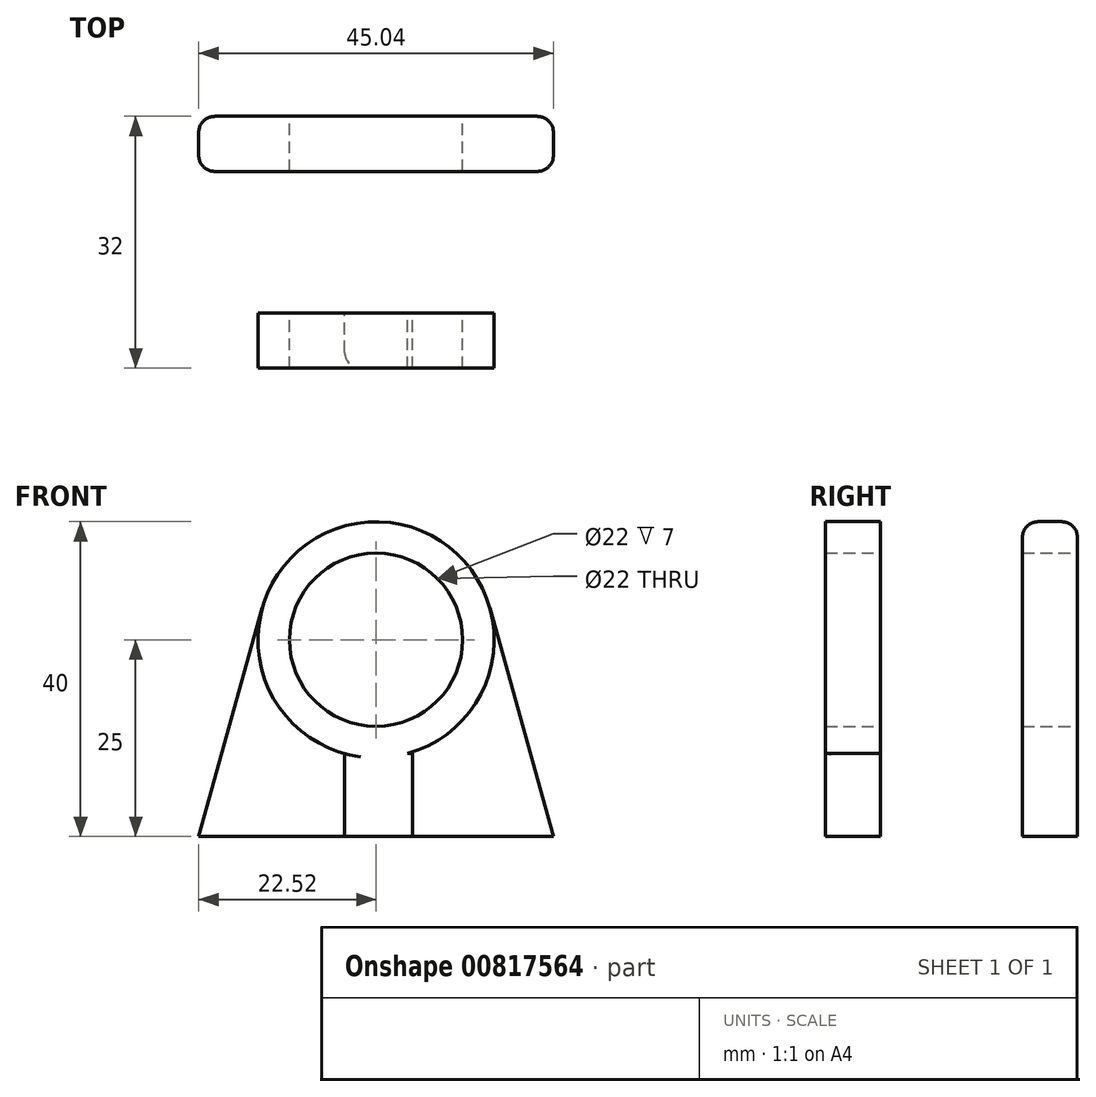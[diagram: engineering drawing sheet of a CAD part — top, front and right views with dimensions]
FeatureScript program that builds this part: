
annotation { "Feature Type Name" : "Feature", "Feature Type Description" : "" }
export const myFeature = defineFeature(function(context is Context, id is Id, definition is map)
    precondition{}
    {
        {
            var Q0;
            Q0=qCreatedBy(makeId("Front.planeOp"),FACE);
            var sketch = newSketch(context, id + "F0", { "sketchPlane" : qUnion([Q0])});
            skCircle(sketch, "E0", {"center": v(0, 25) * mm, "radius": 11 * mm});
            skCircle(sketch, "E1", {"center": v(0, 25) * mm, "radius": 15 * mm});
            skLineSegment(sketch, "E2", {"start": v(-14.45, 29.02) * mm, "end": v(-22.52, 0) * mm});
            skLineSegment(sketch, "E3", {"start": v(-22.52, 0) * mm, "end": v(0, 0) * mm});
            skLineSegment(sketch, "E4", {"start": v(0, 0) * mm, "end": v(0, 11.14) * mm, "construction": true});
            skLineSegment(sketch, "E5.MirrorCS", {"start": v(14.45, 29.02) * mm, "end": v(22.52, 0) * mm});
            skLineSegment(sketch, "E6.MirrorCS", {"start": v(22.52, 0) * mm, "end": v(0, 0) * mm});
            skSolve(sketch);
        }
        {
            assignVariable(context, id + "F1", {"name" : "Thickness", "anyValue" : 7 * mm});
        }
        {
            var Q0;
            {var subQ1=sQuery(id+"F0.wireOp",EDGE,"E2");Q0=makeQuery(id+"F0.imprint","IMPRINT",FACE,{"disambiguationData":[TD([[makeQuery(id+"F0.imprint","IMPRINT",EDGE,{"derivedFrom":subQ1}),1.0]])]});}
            var Q1;
            Q1=makeQuery(id+"F0.imprint","IMPRINT",FACE,{"disambiguationData":[TD([[makeQuery(id+"F0.imprint","IMPRINT",EDGE,{"derivedFrom":sQuery(id+"F0.wireOp",EDGE,"E0")}),-1.0]])]});
            extrude(context, id + "F2", {"entities" : qUnion([Q0, Q1]), "depth" : getVariable(context, 'Thickness'), "offsetDistance" : 25 * mm});
        }
        {
            var Q0;
            Q0=qCreatedBy(makeId("Front.planeOp"),FACE);
            cPlane(context, id + "F3", {"entities" : qUnion([Q0]), "cplaneType" : CPlaneType.OFFSET, "offset" : 25 * mm, "width" : 150 * mm, "height" : 150 * mm});
        }
        {
            var Q0;
            Q0=qCreatedBy(id+"F3.planeOp",FACE);
            var sketch = newSketch(context, id + "F4", { "sketchPlane" : qUnion([Q0])});
            skCircle(sketch, "E7.0", {"center": v(0, 25) * mm, "radius": 11 * mm});
            skCircle(sketch, "E8", {"center": v(0, 25) * mm, "radius": 15 * mm});
            skLineSegment(sketch, "E9.bottom", {"start": v(-3.98, 10.54) * mm, "end": v(4.64, 10.54) * mm});
            skLineSegment(sketch, "E9.top", {"start": v(-3.98, 0) * mm, "end": v(4.64, 0) * mm});
            skLineSegment(sketch, "E9.left", {"start": v(-3.98, 10.54) * mm, "end": v(-3.98, 0) * mm});
            skLineSegment(sketch, "E9.right", {"start": v(4.64, 10.54) * mm, "end": v(4.64, 0) * mm});
            skSolve(sketch);
        }
        {
            var Q0;
            Q0 = qSketchRegion(id + "F4", true);
            extrude(context, id + "F5", {"entities" : qUnion([Q0]), "depth" : getVariable(context, 'Thickness'), "offsetDistance" : 25 * mm});
        }
        {
            var Q0;
            Q0=makeQuery(id+"F2.opExtrude","CAP_EDGE",EDGE,{"disambiguationData":[OSD([sQuery(id+"F0.wireOp",EDGE,"E2")])],"isStart":false});
            var Q1;
            Q1=makeQuery(id+"F2.opExtrude","CAP_EDGE",EDGE,{"disambiguationData":[OSD([sQuery(id+"F0.wireOp",EDGE,"E5.MirrorCS")])],"isStart":true});
            var Q2;
            Q2=makeQuery(id+"F5.opExtrude","CAP_EDGE",EDGE,{"disambiguationData":[OSD([sQuery(id+"F4.wireOp",EDGE,"E9.left")])],"isStart":false});
            fillet(context, id + "F6", {"entities" : qUnion([Q0, Q1, Q2]), "radius" : 2 * mm, "tangentPropagation" : true, "allowEdgeOverflow" : false});
        }
    });
